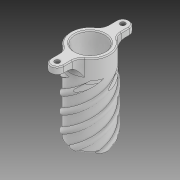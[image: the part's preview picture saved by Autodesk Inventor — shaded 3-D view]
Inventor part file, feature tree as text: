
AUTODESK INVENTOR PART (.ipt)
format: ipt  version: 2020 (Build 240168000, 168)  size: 738,816 bytes
history: native  units: mm
features: sketch x5, revolve x3, fillet x3, pattern_circular x2, other x1, helix x1, extrude x1, chamfer x1, projected_geometry x1
ambient origin geometry x8: Origin, YZ Plane, XZ Plane, XY Plane, X Axis, Y Axis, Z Axis, Center Point
bodies: Solid1 (feature_tree)
feature tree (18):
  revolve  "Revolution1"  [1 undecoded]
  revolve  "Revolution2"  [1 undecoded]
  pattern_circular  "Circular Pattern1"  [2 undecoded]
  sketch  "Sketch3"  dims[d4=90.0deg]
  other  "Work Axis1"
  helix  "Coil1"  [1 undecoded]
  pattern_circular  "Circular Pattern2"  Count=4 Angle=360.0deg
  revolve  "Revolution3"  [1 undecoded]
  fillet  "Fillet2"  Radius=1.5mm
  extrude  "Extrusion1"  Depth=3.0mm
  fillet  "Fillet3"  Radius=0.25mm
  fillet  "Fillet4"  Radius=50.0mm
  chamfer  "Chamfer1"  Distance=1.0mm
  sketch  "Sketch1"  dims[d0=25.0mm d1=4.25mm]
  sketch  "Sketch2"  dims[d2=4.575mm d3=1.425mm]
  projected_geometry  "Projected Loop1"
  sketch  "Sketch4"  dims[d5=0.25mm]
  sketch  "Sketch5"  dims[d6=2.0mm d7=1.3mm d8=90.0deg d9=40.0mm d10=360.0deg d13=6.0mm d14=1.5mm d15=0.75mm d16=0.25mm d17=25.0mm d18=10.0mm d19=7.5mm d20=0.0mm d21=90.0deg d22=90.0deg d23=0.0mm d24=0.0mm d25=50.0mm d26=360.0deg d28=1.0mm d29=1.745329mm d30=90.0deg d31=5.0mm d32=20.0mm d33=2.0mm d34=1.5mm d35=2.0mm d36=0.0mm d37=3.0mm d38=0.5mm d39=0.3mm d40=2.0mm d41=45.0deg]
note: 6 required parameter values undecoded (feature->parameter linkage not recoverable at this tier; creation-order binding heuristic only, values carry confidence <= 0.55)